# Revit family: Lighting_Fixture-Wall-Astro-Digit US
name_source: partatom
category: Lighting Fixtures
revit_build: Autodesk Revit 2018 (Build: 20170927_1515(x64)
units: mm (PartAtom-declared; Revit-internal decimal feet)

## family parameters
Cut with Voids When Loaded = No
Host = Face
Light Source = No
OmniClass Number = 23.80.70.00
OmniClass Title = Lighting
Part Type = Normal
Room Calculation Point = No
Round Connector Dimension = Use Diameter
Shared = No

## types (1)
- Digit
    Apparent Load = 4 VA
    Arm Angle = 25.00°
    Assembly Code = D5020200
    Casing Material = Astro - Zinc - Chrome Finish
    Class = 2
    Description = Recessed Wall Light
    Dimmable = No
    Energy Efficiency Rating = -
    Head Rotation = 135.00°
    Height = 80 mm  [stored 0.262467 ft]
    IP Rating = IP20
    Lamp = LED
    Lamp included = Yes
    Length = 64 mm  [stored 0.209974 ft]
    Light Source Elevation = 1600 mm  [stored 5.24934 ft]
    Light Source From Wall = 350 mm  [stored 1.14829 ft]
    Luminaire Lamp Efficiency Rating = A
    Manufacturer = Astro Lighting Ltd, CM20 2DP
    Model = 7164 Digit Chrome
    Mountable on normally flammable surfaces = Yes
    Number of Poles = 1
    Product Documentation = http://www.astrolighting.co.uk
/kw/7164/7164_Digit
    Rear Casing Material = Astro - ABS - Black
    Suitable for bathroom zone = zone 3
    Type Comments = Includes integral LED driver
Cut out size: 66mm high x 172mm wide
Requires 60mm recess minimum
Includes integral switch
    URL = www.astrolighting.co.uk
    Voltage = 120 V
    Wattage Comments = 2W
    Weight = 1.17 kg
    Width = 190 mm

note: [stored X ft] marks values corroborated as IEEE doubles in the binary element streams (Revit-internal decimal feet)

## geometry (parser evidence)
native form markers: Sweep x6
no freeform markers — native parametric forms only
